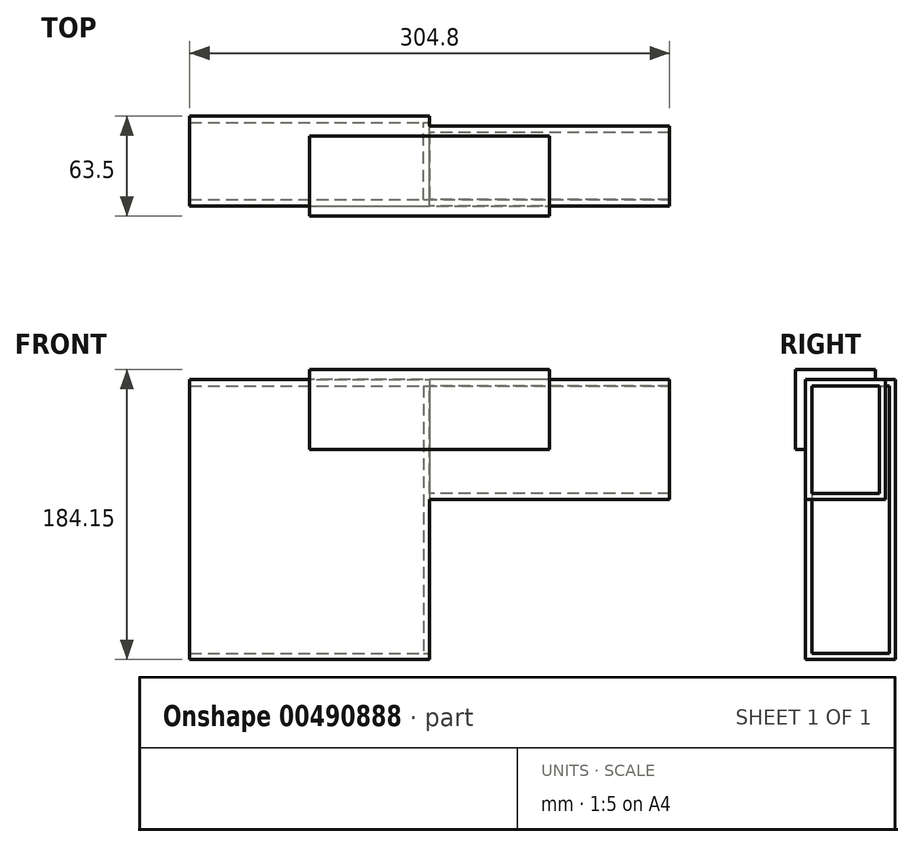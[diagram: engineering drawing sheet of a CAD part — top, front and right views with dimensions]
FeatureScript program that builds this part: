
annotation { "Feature Type Name" : "Feature", "Feature Type Description" : "" }
export const myFeature = defineFeature(function(context is Context, id is Id, definition is map)
    precondition{}
    {
        {
            var Q0;
            Q0=qCreatedBy(makeId("Top.planeOp"),FACE);
            var sketch = newSketch(context, id + "F0", { "sketchPlane" : qUnion([Q0])});
            skLineSegment(sketch, "E0.bottom", {"start": v(0, 0) * mm, "end": v(152.4, 0) * mm});
            skLineSegment(sketch, "E0.top", {"start": v(0, 57.15) * mm, "end": v(152.4, 57.15) * mm});
            skLineSegment(sketch, "E0.left", {"start": v(0, 0) * mm, "end": v(0, 57.15) * mm});
            skLineSegment(sketch, "E0.right", {"start": v(152.4, 0) * mm, "end": v(152.4, 57.15) * mm});
            skSolve(sketch);
        }
        {
            var Q0;
            Q0=makeQuery(id+"F0.imprint","IMPRINT",FACE,{"disambiguationData":[TD([[makeQuery(id+"F0.imprint","IMPRINT",EDGE,{"derivedFrom":sQuery(id+"F0.wireOp",EDGE,"E0.bottom")}),1.0]])]});
            extrude(context, id + "F1", {"entities" : qUnion([Q0]), "depth" : 177.8 * mm});
        }
        {
            var Q0;
            Q0=makeQuery(id+"F1.opExtrude","SWEPT_FACE",FACE,{"disambiguationData":[OSD([sQuery(id+"F0.wireOp",EDGE,"E0.right")])]});
            shell(context, id + "F2", {"entities" : qUnion([Q0]), "thickness" : 4 * mm});
        }
        {
            var Q0;
            Q0=makeQuery(id+"F2.opShell","OFFSET_FACE",FACE,{"disambiguationData":[OSD([sQuery(id+"F0.wireOp",EDGE,"E0.left")])]});
            extrude(context, id + "F3", {"entities" : qUnion([Q0]), "operationType" : NewBodyOperationType.REMOVE, "endBound" : BoundingType.THROUGH_ALL, "oppositeDirection" : true, "depth" : 25.4 * mm});
        }
        {
            var Q0;
            Q0=makeQuery(id+"F1.opExtrude","SWEPT_FACE",FACE,{"disambiguationData":[OSD([sQuery(id+"F0.wireOp",EDGE,"E0.right")])]});
            cPlane(context, id + "F4", {"entities" : qUnion([Q0]), "cplaneType" : CPlaneType.OFFSET, "offset" : 0 * mm, "width" : 152.4 * mm, "height" : 152.4 * mm});
        }
        {
            var Q0;
            Q0=qCreatedBy(id+"F4.planeOp",FACE);
            var sketch = newSketch(context, id + "F5", { "sketchPlane" : qUnion([Q0])});
            skLineSegment(sketch, "E1.bottom", {"start": v(3.99, 173.81) * mm, "end": v(53.16, 173.81) * mm});
            skLineSegment(sketch, "E1.top", {"start": v(3.99, 3.99) * mm, "end": v(53.16, 3.99) * mm});
            skLineSegment(sketch, "E1.left", {"start": v(3.99, 173.81) * mm, "end": v(3.99, 3.99) * mm});
            skLineSegment(sketch, "E1.right", {"start": v(53.16, 173.81) * mm, "end": v(53.16, 3.99) * mm});
            skSolve(sketch);
        }
        {
            var Q0;
            Q0 = qSketchRegion(id + "F5", true);
            extrude(context, id + "F6", {"entities" : qUnion([Q0]), "oppositeDirection" : true, "depth" : 4 * mm});
        }
        {
            var Q0;
            Q0=qCreatedBy(id+"F4.planeOp",FACE);
            var sketch = newSketch(context, id + "F7", { "sketchPlane" : qUnion([Q0])});
            skLineSegment(sketch, "E2.bottom", {"start": v(0, 177.8) * mm, "end": v(50.8, 177.8) * mm});
            skLineSegment(sketch, "E2.top", {"start": v(0, 101.6) * mm, "end": v(50.8, 101.6) * mm});
            skLineSegment(sketch, "E2.left", {"start": v(0, 177.8) * mm, "end": v(0, 101.6) * mm});
            skLineSegment(sketch, "E2.right", {"start": v(50.8, 177.8) * mm, "end": v(50.8, 101.6) * mm});
            skSolve(sketch);
        }
        {
            var Q0;
            Q0=makeQuery(id+"F7.imprint","IMPRINT",FACE,{"disambiguationData":[TD([[makeQuery(id+"F7.imprint","IMPRINT",EDGE,{"derivedFrom":sQuery(id+"F7.wireOp",EDGE,"E2.bottom")}),-1.0]])]});
            extrude(context, id + "F8", {"entities" : qUnion([Q0]), "depth" : 152.4 * mm});
        }
        {
            var Q0;
            Q0=makeQuery(id+"F8.opExtrude","CAP_FACE",FACE,{"disambiguationData":[OSD([sQuery(id+"F7.wireOp",EDGE,"E2.bottom"),sQuery(id+"F7.wireOp",EDGE,"E2.top"),sQuery(id+"F7.wireOp",EDGE,"E2.left"),sQuery(id+"F7.wireOp",EDGE,"E2.right")])],"isStart":false});
            shell(context, id + "F9", {"entities" : qUnion([Q0]), "thickness" : 4 * mm});
        }
        {
            var Q0;
            Q0=makeQuery(id+"F9.opShell","OFFSET_FACE",FACE,{"disambiguationData":[OSD([sQuery(id+"F7.wireOp",EDGE,"E2.bottom"),sQuery(id+"F7.wireOp",EDGE,"E2.top"),sQuery(id+"F7.wireOp",EDGE,"E2.left"),sQuery(id+"F7.wireOp",EDGE,"E2.right")])]});
            extrude(context, id + "F10", {"entities" : qUnion([Q0]), "operationType" : NewBodyOperationType.REMOVE, "endBound" : BoundingType.UP_TO_NEXT, "oppositeDirection" : true, "depth" : 25.4 * mm});
        }
        {
            var Q0;
            Q0=makeQuery(id+"F1.opExtrude","CAP_FACE",FACE,{"disambiguationData":[OSD([sQuery(id+"F0.wireOp",EDGE,"E0.bottom"),sQuery(id+"F0.wireOp",EDGE,"E0.top"),sQuery(id+"F0.wireOp",EDGE,"E0.left"),sQuery(id+"F0.wireOp",EDGE,"E0.right")])],"isStart":false});
            var Q1;
            Q1=makeQuery(id+"F8.opExtrude","SWEPT_FACE",FACE,{"disambiguationData":[OSD([sQuery(id+"F7.wireOp",EDGE,"E2.bottom")])]});
            cPlane(context, id + "F11", {"entities" : qUnion([Q0, Q1]), "cplaneType" : CPlaneType.MID_PLANE, "offset" : 25.4 * mm, "width" : 152.4 * mm, "height" : 152.4 * mm});
        }
        {
            var Q0;
            Q0=qCreatedBy(id+"F11.planeOp",FACE);
            var sketch = newSketch(context, id + "F12", { "sketchPlane" : qUnion([Q0])});
            skLineSegment(sketch, "E3.bottom", {"start": v(228.6, 44.45) * mm, "end": v(76.2, 44.45) * mm});
            skLineSegment(sketch, "E3.top", {"start": v(228.6, -6.35) * mm, "end": v(76.2, -6.35) * mm});
            skLineSegment(sketch, "E3.left", {"start": v(228.6, 44.45) * mm, "end": v(228.6, -6.35) * mm});
            skLineSegment(sketch, "E3.right", {"start": v(76.2, 44.45) * mm, "end": v(76.2, -6.35) * mm});
            skSolve(sketch);
        }
        {
            var Q0;
            Q0=makeQuery(id+"F12.imprint","IMPRINT",FACE,{"disambiguationData":[TD([[makeQuery(id+"F12.imprint","IMPRINT",EDGE,{"derivedFrom":sQuery(id+"F12.wireOp",EDGE,"E3.bottom")}),1.0]])]});
            extrude(context, id + "F13", {"entities" : qUnion([Q0]), "depth" : 6.35 * mm});
        }
        {
            var Q0;
            Q0=makeQuery(id+"F13.opExtrude","CAP_FACE",FACE,{"disambiguationData":[OSD([sQuery(id+"F12.wireOp",EDGE,"E3.bottom"),sQuery(id+"F12.wireOp",EDGE,"E3.top"),sQuery(id+"F12.wireOp",EDGE,"E3.left"),sQuery(id+"F12.wireOp",EDGE,"E3.right")])],"isStart":true});
            var sketch = newSketch(context, id + "F14", { "sketchPlane" : qUnion([Q0])});
            skLineSegment(sketch, "E4.bottom", {"start": v(76.2, 6.35) * mm, "end": v(228.6, 6.35) * mm});
            skLineSegment(sketch, "E4.top", {"start": v(76.2, 0) * mm, "end": v(228.6, 0) * mm});
            skLineSegment(sketch, "E4.left", {"start": v(76.2, 6.35) * mm, "end": v(76.2, 0) * mm});
            skLineSegment(sketch, "E4.right", {"start": v(228.6, 6.35) * mm, "end": v(228.6, 0) * mm});
            skSolve(sketch);
        }
        {
            var Q0;
            Q0=makeQuery(id+"F14.imprint","IMPRINT",FACE,{"disambiguationData":[TD([[makeQuery(id+"F14.imprint","IMPRINT",EDGE,{"derivedFrom":sQuery(id+"F14.wireOp",EDGE,"E4.bottom")}),1.0]])]});
            extrude(context, id + "F15", {"entities" : qUnion([Q0]), "operationType" : NewBodyOperationType.ADD, "depth" : 44.45 * mm});
        }
    });
